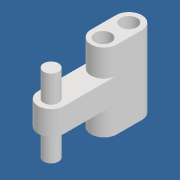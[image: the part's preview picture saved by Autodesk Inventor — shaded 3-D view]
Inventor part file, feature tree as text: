
AUTODESK INVENTOR PART (.ipt)
format: ipt  version: 2020 (Build 240168000, 168)  size: 146,944 bytes
history: native  units: mm
features: extrude x3, fillet x3, sketch x3
ambient origin geometry x8: Origin, YZ Plane, XZ Plane, XY Plane, X Axis, Y Axis, Z Axis, Center Point
bodies: Solid1 (feature_tree)
feature tree (9):
  extrude  "Extrusion1"  Depth=15.7mm
  fillet  "Fillet1"  Radius=5.0mm
  fillet  "Fillet2"  Radius=5.0mm
  extrude  "Extrusion2"  Depth=24.0mm TaperAngle=0.0deg
  extrude  "Extrusion4"  Depth=4.0mm
  fillet  "Fillet3"  Radius=4.0mm
  sketch  "Sketch1"  dims[d0=8.0mm d1=15.7mm d4=5.0mm d5=5.0mm]
  sketch  "Sketch2"  dims[d8=8.0mm d11=24.0mm d12=0.0mm]
  sketch  "Sketch4"  dims[d13=4.0mm d14=4.0mm d15=4.0mm d17=20.3mm d18=7.4mm d19=8.3mm d20=8.0mm d21=0.0mm d24=4.6mm d25=4.0mm d26=4.0mm d27=8.3mm d28=15.7mm d29=0.0mm d30=0.0mm d31=4.0mm]
